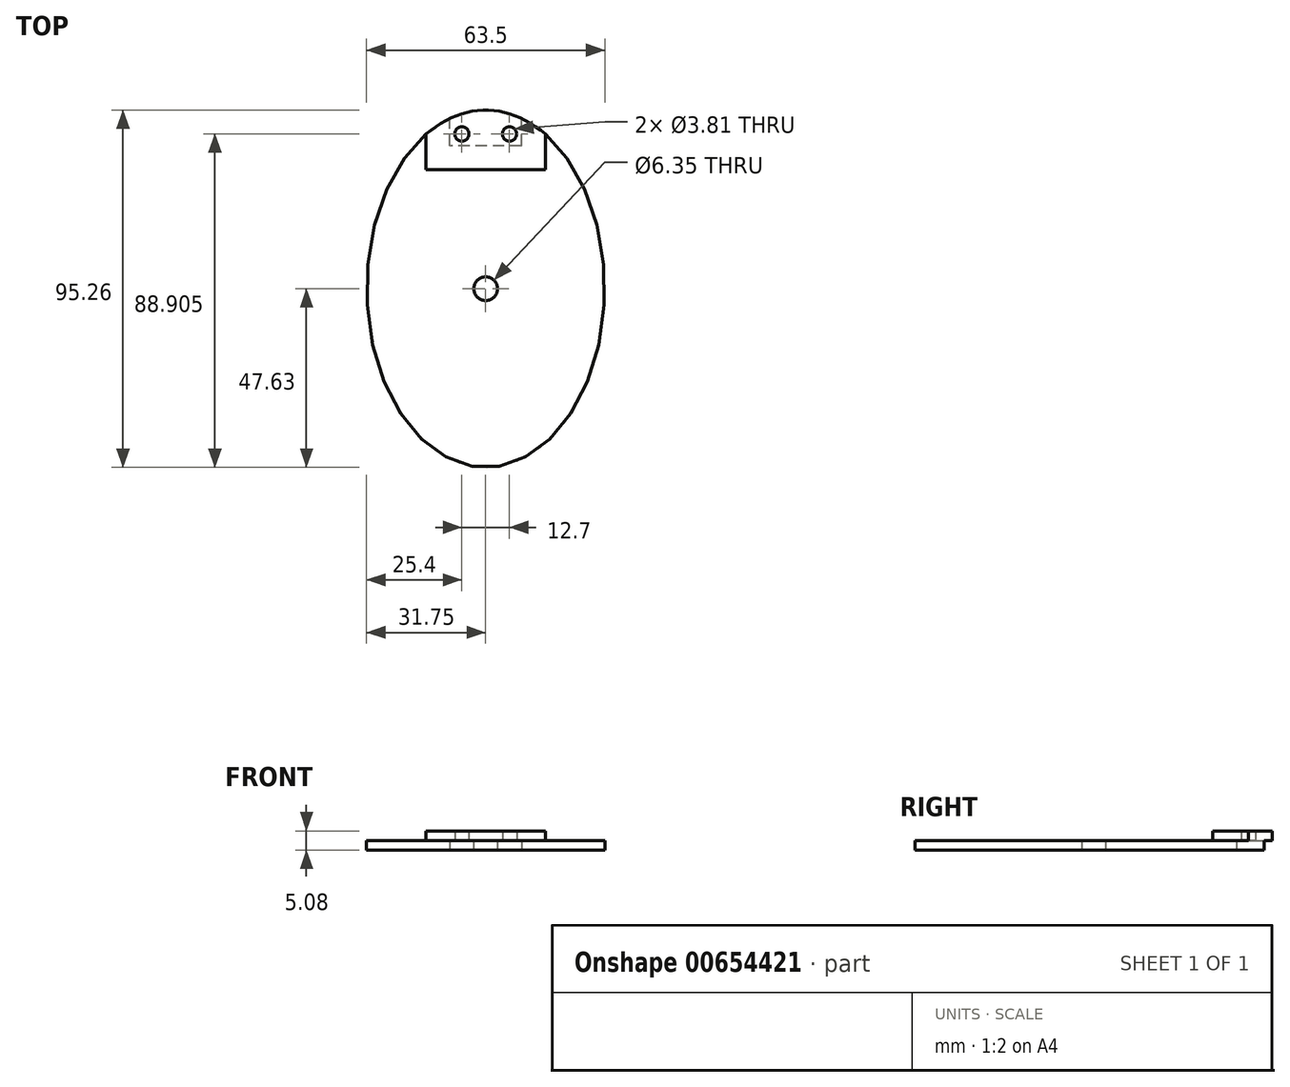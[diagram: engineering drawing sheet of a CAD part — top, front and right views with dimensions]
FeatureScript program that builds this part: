
annotation { "Feature Type Name" : "Feature", "Feature Type Description" : "" }
export const myFeature = defineFeature(function(context is Context, id is Id, definition is map)
    precondition{}
    {
        {
            var Q0;
            Q0=qCreatedBy(makeId("Top.planeOp"),FACE);
            var sketch = newSketch(context, id + "F0", { "sketchPlane" : qUnion([Q0])});
            skEllipse(sketch, "E0", {"center": v(0, 0) * mm, "majorRadius": 47.63 * mm, "minorRadius": 31.75 * mm, "majorAxis": v(0, -1)});
            skCircle(sketch, "E1", {"center": v(0, 0) * mm, "radius": 3.18 * mm});
            skLineSegment(sketch, "E2", {"start": v(0, 0) * mm, "end": v(0, 41.28) * mm, "construction": true});
            skPoint(sketch, "E2.endSnap0", {"position": v(0, 47.63) * mm});
            skLineSegment(sketch, "E3", {"start": v(0, 41.28) * mm, "end": v(6.35, 41.28) * mm, "construction": true});
            skCircle(sketch, "E4", {"center": v(6.35, 41.28) * mm, "radius": 1.9 * mm});
            skCircle(sketch, "E5.MirrorC", {"center": v(-6.35, 41.28) * mm, "radius": 1.9 * mm});
            skSolve(sketch);
        }
        {
            var Q0;
            Q0=makeQuery(id+"F0.imprint","IMPRINT",FACE,{"disambiguationData":[TD([[makeQuery(id+"F0.imprint","IMPRINT",EDGE,{"derivedFrom":sQuery(id+"F0.wireOp",EDGE,"E0")}),1.0]])]});
            extrude(context, id + "F1", {"entities" : qUnion([Q0]), "depth" : 2.54 * mm, "offsetDistance" : 25.4 * mm});
        }
        {
            var Q0;
            Q0=makeQuery(id+"F1.opExtrude","CAP_FACE",FACE,{"disambiguationData":[OSD([sQuery(id+"F0.wireOp",EDGE,"E0"),sQuery(id+"F0.wireOp",EDGE,"E1"),sQuery(id+"F0.wireOp",EDGE,"E4"),sQuery(id+"F0.wireOp",EDGE,"E5.MirrorC")])],"isStart":false});
            var sketch = newSketch(context, id + "F2", { "sketchPlane" : qUnion([Q0])});
            skLineSegment(sketch, "E6", {"start": v(0, 0) * mm, "end": v(0, 31.75) * mm, "construction": true});
            skLineSegment(sketch, "E7", {"start": v(0, 31.75) * mm, "end": v(-15.88, 31.75) * mm});
            skEllipticalArc(sketch, "E8.0", {});
            skLineSegment(sketch, "E9", {"start": v(-15.88, 31.75) * mm, "end": v(-15.88, 41.24) * mm});
            skLineSegment(sketch, "E10.MirrorCS", {"start": v(0, 31.75) * mm, "end": v(15.88, 31.75) * mm});
            skLineSegment(sketch, "E11.MirrorCS", {"start": v(15.88, 31.75) * mm, "end": v(15.88, 41.24) * mm});
            skCircle(sketch, "E12.0", {"center": v(-6.35, 41.28) * mm, "radius": 1.9 * mm});
            skCircle(sketch, "E13.0", {"center": v(6.35, 41.28) * mm, "radius": 1.9 * mm});
            const initialGuessF2  = {"E8.0": [0, 0, 0, -1, 0.047625, 0.03175, 2.6179938779914944, 3.665191429188092]};
            skSetInitialGuess(sketch, initialGuessF2);
            skSolve(sketch);
        }
        {
            var Q0;
            Q0=makeQuery(id+"F2.imprint","IMPRINT",FACE,{"disambiguationData":[TD([[makeQuery(id+"F2.imprint","IMPRINT",EDGE,{"derivedFrom":sQuery(id+"F2.wireOp",EDGE,"E7")}),-1.0]])]});
            extrude(context, id + "F3", {"entities" : qUnion([Q0]), "operationType" : NewBodyOperationType.ADD, "depth" : 2.54 * mm, "offsetDistance" : 25.4 * mm});
        }
        {
            var Q0;
            Q0=makeQuery(id+"F1.opExtrude","CAP_FACE",FACE,{"disambiguationData":[OSD([sQuery(id+"F0.wireOp",EDGE,"E0"),sQuery(id+"F0.wireOp",EDGE,"E1"),sQuery(id+"F0.wireOp",EDGE,"E4"),sQuery(id+"F0.wireOp",EDGE,"E5.MirrorC")])],"isStart":true});
            var sketch = newSketch(context, id + "F4", { "sketchPlane" : qUnion([Q0])});
            skLineSegment(sketch, "E14", {"start": v(0, 0) * mm, "end": v(0, -38.1) * mm, "construction": true});
            skLineSegment(sketch, "E15", {"start": v(0, -38.1) * mm, "end": v(-9.52, -38.1) * mm});
            skLineSegment(sketch, "E16", {"start": v(-9.52, -38.1) * mm, "end": v(-9.52, -45.43) * mm});
            skLineSegment(sketch, "E17.MirrorCS", {"start": v(0, -38.1) * mm, "end": v(9.52, -38.1) * mm});
            skLineSegment(sketch, "E18.MirrorCS", {"start": v(9.52, -38.1) * mm, "end": v(9.52, -45.43) * mm});
            skEllipse(sketch, "E19.0", {"center": v(0, 0) * mm, "majorRadius": 47.63 * mm, "minorRadius": 31.75 * mm, "majorAxis": v(0, 1)});
            skSolve(sketch);
        }
        {
            var Q0;
            Q0=makeQuery(id+"F4.imprint","IMPRINT",FACE,{"disambiguationData":[TD([[makeQuery(id+"F4.imprint","IMPRINT",EDGE,{"derivedFrom":sQuery(id+"F4.wireOp",EDGE,"E15")}),1.0]])]});
            extrude(context, id + "F5", {"entities" : qUnion([Q0]), "operationType" : NewBodyOperationType.REMOVE, "oppositeDirection" : true, "depth" : 2.54 * mm, "offsetDistance" : 25.4 * mm});
        }
    });
